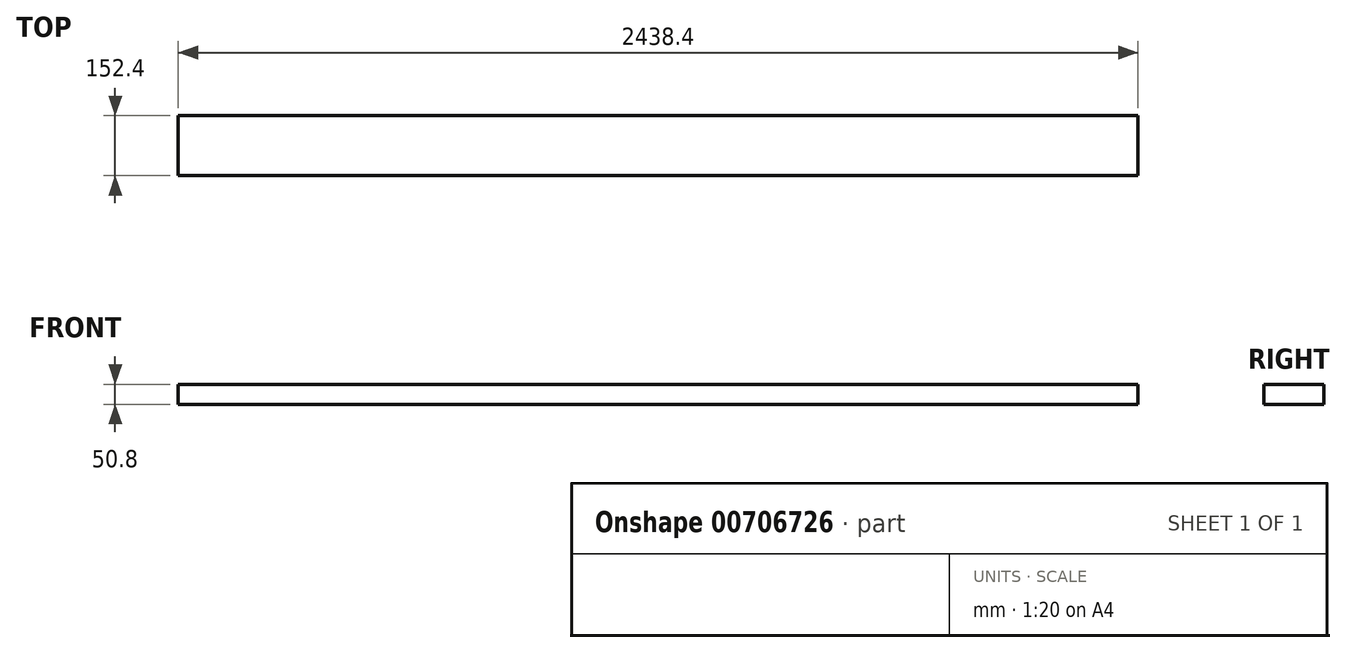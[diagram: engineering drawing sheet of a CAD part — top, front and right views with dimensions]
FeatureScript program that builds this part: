
annotation { "Feature Type Name" : "Feature", "Feature Type Description" : "" }
export const myFeature = defineFeature(function(context is Context, id is Id, definition is map)
    precondition{}
    {
        {
            var Q0;
            Q0=qCreatedBy(makeId("Top.planeOp"),FACE);
            var sketch = newSketch(context, id + "F0", { "sketchPlane" : qUnion([Q0])});
            skLineSegment(sketch, "E0.bottom", {"start": v(-1219.2, 76.2) * mm, "end": v(1219.2, 76.2) * mm});
            skLineSegment(sketch, "E0.top", {"start": v(-1219.2, -76.2) * mm, "end": v(1219.2, -76.2) * mm});
            skLineSegment(sketch, "E0.left", {"start": v(-1219.2, 76.2) * mm, "end": v(-1219.2, -76.2) * mm});
            skLineSegment(sketch, "E0.right", {"start": v(1219.2, 76.2) * mm, "end": v(1219.2, -76.2) * mm});
            skPoint(sketch, "E0.middle", {"position": v(0, 0) * mm});
            skSolve(sketch);
        }
        {
            var Q0;
            Q0=makeQuery(id+"F0.imprint","IMPRINT",FACE,{"disambiguationData":[TD([[makeQuery(id+"F0.imprint","IMPRINT",EDGE,{"derivedFrom":sQuery(id+"F0.wireOp",EDGE,"E0.bottom")}),-1.0]])]});
            extrude(context, id + "F1", {"entities" : qUnion([Q0]), "depth" : 50.8 * mm, "offsetDistance" : 25.4 * mm});
        }
    });
